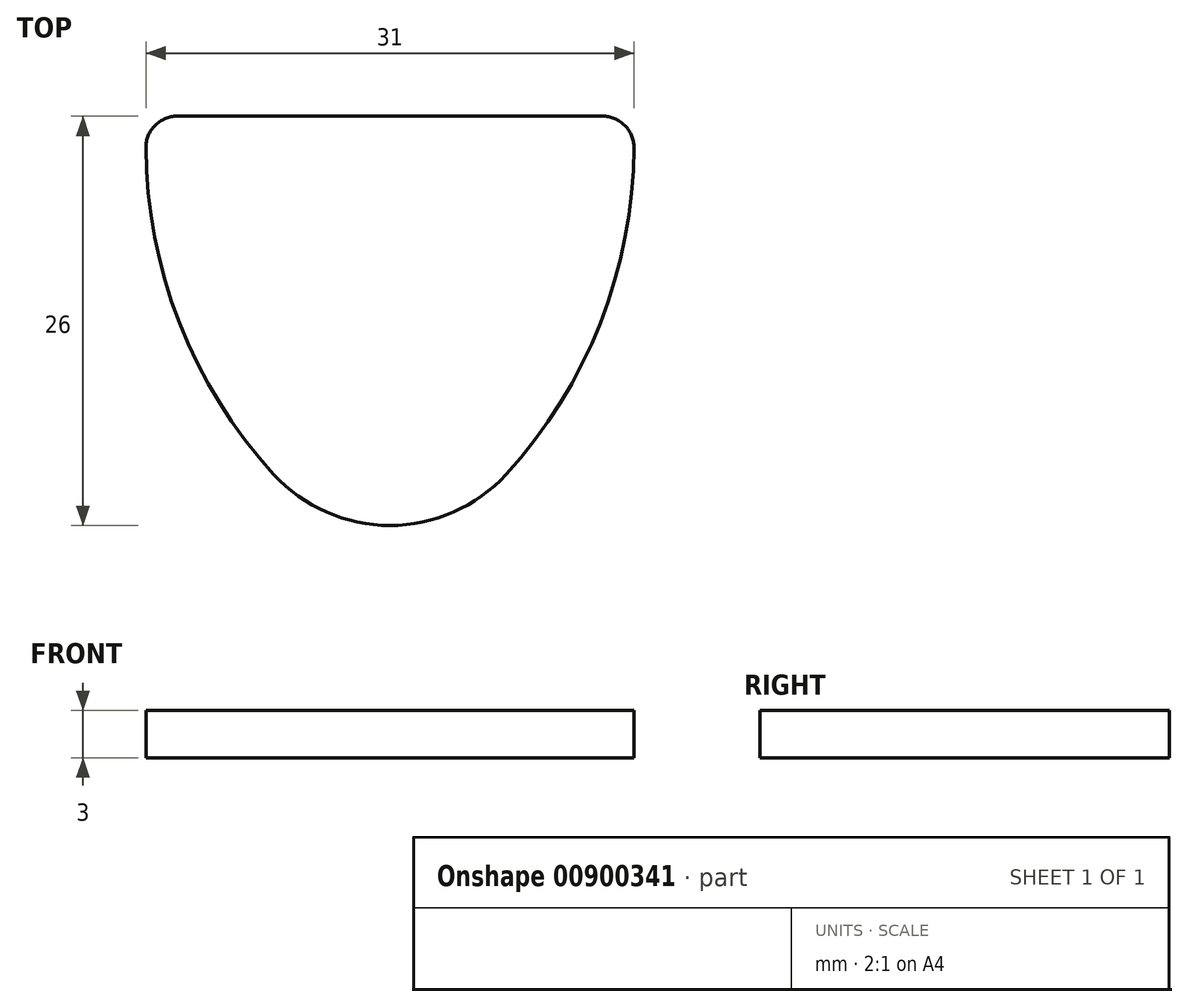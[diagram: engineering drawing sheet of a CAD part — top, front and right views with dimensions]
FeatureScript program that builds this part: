
annotation { "Feature Type Name" : "Feature", "Feature Type Description" : "" }
export const myFeature = defineFeature(function(context is Context, id is Id, definition is map)
    precondition{}
    {
        {
            var Q0;
            Q0=qCreatedBy(makeId("Top.planeOp"),FACE);
            var sketch = newSketch(context, id + "F0", { "sketchPlane" : qUnion([Q0])});
            skLineSegment(sketch, "E0", {"start": v(-13.5, 0) * mm, "end": v(0, 0) * mm});
            skLineSegment(sketch, "E1", {"start": v(0, 0) * mm, "end": v(13.5, 0) * mm});
            skArc(sketch, "E2", {"start": v(7.38, -22.75) * mm, "mid": v(13.37, -13.13) * mm, "end": v(15.5, -2.01) * mm});
            skArc(sketch, "E3", {"start": v(-15.5, -2.01) * mm, "mid": v(-13.37, -13.13) * mm, "end": v(-7.38, -22.75) * mm});
            skArc(sketch, "E4", {"start": v(-7.38, -22.75) * mm, "mid": v(0, -26) * mm, "end": v(7.38, -22.75) * mm});
            skPoint(sketch, "E5.visualSharp", {"position": v(-15.45, 0) * mm});
            skArc(sketch, "E5.filletArc", {"start": v(-13.5, 0) * mm, "mid": v(-14.92, -0.59) * mm, "end": v(-15.5, -2.01) * mm});
            skPoint(sketch, "E6.visualSharp", {"position": v(15.45, 0) * mm});
            skArc(sketch, "E6.filletArc", {"start": v(15.5, -2.01) * mm, "mid": v(14.92, -0.59) * mm, "end": v(13.5, 0) * mm});
            skPoint(sketch, "E7", {"position": v(0, -14) * mm});
            skCircle(sketch, "E8", {"center": v(-13.5, -2) * mm, "radius": 2 * mm, "construction": true});
            skSolve(sketch);
        }
        {
            var Q0;
            Q0 = qSketchRegion(id + "F0", true);
            extrude(context, id + "F1", {"entities" : qUnion([Q0]), "depth" : 3 * mm, "offsetDistance" : 25 * mm});
        }
    });
